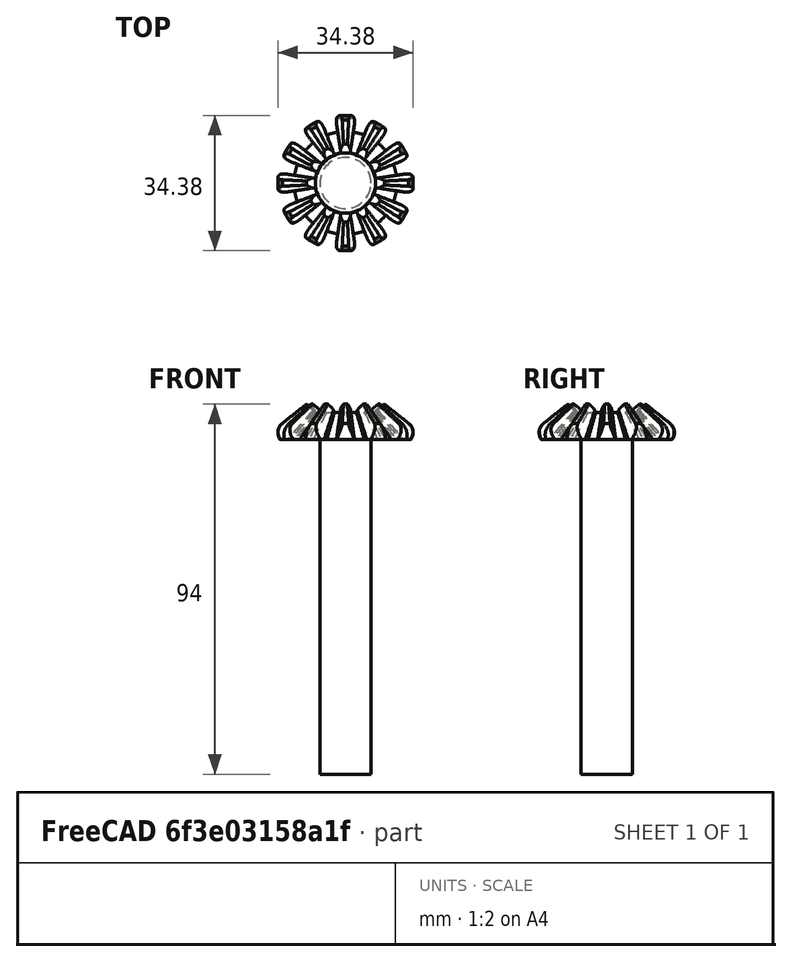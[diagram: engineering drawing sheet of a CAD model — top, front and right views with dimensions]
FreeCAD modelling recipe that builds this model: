
FCSTD DOCUMENT  (FreeCAD 1.0R39319 (Git))
Label: DG Krushna gearshaft
License: All rights reserved
LicenseURL: https://en.wikipedia.org/wiki/All_rights_reserved
objects: Sketcher::SketchObject×5, TechDraw::DrawViewDimension×5, TechDraw::DrawProjGroupItem×4, PartDesign::Groove×3, TechDraw::DrawSVGTemplate×2, TechDraw::DrawProjGroup×2, TechDraw::DrawPage×2, Part::FeaturePython×1, PartDesign::FeatureBase×1, PartDesign::Pad×1, PartDesign::Body×1
note: 31 computed .brp shape members not serialized (recipe doc carries the construction recipe); baked Part::Feature solids carry a one-line shape summary decoded from their .brp

FEATURE [Part::FeaturePython] BevelGear  # WARN: FeaturePython — macro-defined, semantics opaque (R4)
  AttacherType = Attacher::AttachEngine3D
  angular_backlash = 0
  backlash = 0
  beta = 0
  clearance = 0.1
  dw = 33.6
  height = 9
  module = 2.8
  num_teeth = 12
  numpoints = 20
  pitch_angle = 45
  pressure_angle = 20
  reset_origin = true
  version = 1.3.0
  expr: angular_backlash = backlash / dw * 360 ° / pi
  expr: dw = num_teeth * module
FEATURE [PartDesign::FeatureBase] BaseFeature
  BaseFeature = -> BevelGear
  Suppressed = false
FEATURE [Sketcher::SketchObject] Sketch001
  ArcFitTolerance = 1e-06
  FullyConstrained = true
  MakeInternals = false
  MapMode = 5
  Placement = pos=(0,0,0) rot=(1,0,0;3.14159rad)
  sketch-geometry (2):
    g0: Circle CenterX=0 CenterY=0 CenterZ=0 NormalX=0 NormalY=0 NormalZ=1 AngleXU=0 Radius=16.6594
    g1: Circle CenterX=0 CenterY=0 CenterZ=0 NormalX=0 NormalY=0 NormalZ=1 AngleXU=0 Radius=24.4797
  constraints (4):
    c: Coincident(g0,g-1)
    c: PointOnObject(g-4,g0)
    c: Coincident(g1,g0)
    c: PointOnObject(g-3,g1)
FEATURE [Sketcher::SketchObject] Sketch002
  ArcFitTolerance = 1e-06
  AttachmentSupport = -> [YZ_Plane]
  ExternalGeometry = -> [Sketch001]
  FullyConstrained = true
  MakeInternals = false
  MapMode = 5
  Placement = pos=(0,0,0) rot=(0.57735,0.57735,0.57735;2.0944rad)
  sketch-geometry (3):
    g0: LineSegment StartX=16.6594 StartY=0 StartZ=0 EndX=24.4797 EndY=7.82034 EndZ=0
    g1: LineSegment StartX=24.4797 StartY=0 StartZ=0 EndX=24.4797 EndY=7.82034 EndZ=0
    g2: LineSegment StartX=24.4797 StartY=0 StartZ=0 EndX=16.6594 EndY=0 EndZ=0
  constraints (7):
    c: Coincident(g0,g-3)
    c: Coincident(g1,g-4)
    c: Vertical(g1)
    c: Coincident(g0,g1)
    c: Angle(g-4,g0) = 0.785398
    c: Coincident(g2,g1)
    c: Coincident(g2,g0)
FEATURE [PartDesign::Groove] Groove001
  Angle = 360
  Angle2 = 60
  Axis = (0,0,1)
  Base = (0,0,0)
  BaseFeature = -> BaseFeature
  Profile = -> Sketch002
  ReferenceAxis = -> Sketch002 [V_Axis]
  Refine = true
  Suppressed = false
  Type = 0
FEATURE [Sketcher::SketchObject] Sketch
  ArcFitTolerance = 1e-06
  AttachmentSupport = -> [XZ_Plane]
  ExternalGeometry = -> [Groove001]
  FullyConstrained = true
  MakeInternals = false
  MapMode = 5
  Placement = pos=(0,0,0) rot=(1,0,0;1.5708rad)
  sketch-geometry (4):
    g0: LineSegment StartX=9.88232 StartY=9 StartZ=0 EndX=0 EndY=9 EndZ=0
    g1: LineSegment StartX=9.88232 StartY=9 StartZ=0 EndX=7.63232 EndY=6.75 EndZ=0
    g2: LineSegment StartX=7.63232 StartY=6.75 StartZ=0 EndX=0 EndY=6.75 EndZ=0
    g3: LineSegment StartX=0 StartY=9 StartZ=0 EndX=0 EndY=6.75 EndZ=0
  constraints (11):
    c: Coincident(g0,g-3)
    c: PointOnObject(g0,g-2)
    c: Horizontal(g0)
    c: Coincident(g1,g0)
    c: Coincident(g2,g1)
    c: Horizontal(g2)
    c: Coincident(g3,g0)
    c: Coincident(g3,g2)
    c: Vertical(g3)
    c: Angle(g0,g1) = 0.785398
    c: DistanceY(g3,g3) = 2.25
FEATURE [PartDesign::Groove] Groove
  Angle = 360
  Angle2 = 60
  Axis = (0,2e-16,1)
  Base = (0,0,0)
  BaseFeature = -> Groove001
  Profile = -> Sketch
  ReferenceAxis = -> Sketch [V_Axis]
  Refine = true
  Suppressed = false
  Type = 0
FEATURE [Sketcher::SketchObject] Sketch003
  ArcFitTolerance = 1e-06
  FullyConstrained = true
  MakeInternals = false
  MapMode = 5
  Placement = pos=(0,0,0) rot=(1,0,0;3.14159rad)
  sketch-geometry (1):
    g0: Circle CenterX=0 CenterY=0 CenterZ=0 NormalX=0 NormalY=0 NormalZ=1 AngleXU=0 Radius=6.5
  constraints (2):
    c: Diameter(g0) = 13
    c: Coincident(g0,g-1)
FEATURE [PartDesign::Pad] Pad
  BaseFeature = -> Groove
  Direction = (0,-1e-16,-1)
  Length = 85
  Length2 = 10
  Profile = -> Sketch003
  ReferenceAxis = -> Sketch003 [N_Axis]
  Refine = true
  Suppressed = false
  Type = 0
FEATURE [Sketcher::SketchObject] Sketch004
  ArcFitTolerance = 1e-06
  AttachmentSupport = -> [YZ_Plane]
  ExternalGeometry = -> [Pad]
  FullyConstrained = true
  MakeInternals = false
  MapMode = 5
  Placement = pos=(0,0,0) rot=(0.57735,0.57735,0.57735;2.0944rad)
  sketch-geometry (5):
    g0: LineSegment StartX=18.6998 StartY=2.04045 StartZ=0 EndX=16.314 EndY=-0.345337 EndZ=0
    g1: ArcOfCircle CenterX=14.1927 CenterY=1.77598 CenterZ=0 NormalX=0 NormalY=0 NormalZ=1 AngleXU=0 Radius=3 StartAngle=5.49779 EndAngle=7.18581
    g2: LineSegment StartX=16.0514 StartY=4.13084 StartZ=0 EndX=18.1868 EndY=6.26631 EndZ=0
    g3: LineSegment StartX=18.1868 StartY=6.26631 StartZ=0 EndX=20.8353 EndY=4.17592 EndZ=0
    g4: LineSegment StartX=20.8353 StartY=4.17592 StartZ=0 EndX=18.6998 EndY=2.04045 EndZ=0
  constraints (13):
    c: Coincident(g0,g-4)
    c: Tangent(g1,g-4)
    c: Tangent(g0,g1) = 1.5708
    c: Radius(g1) = 3
    c: Coincident(g2,g1)
    c: Coincident(g3,g2)
    c: Coincident(g4,g0)
    c: Coincident(g4,g3)
    c: Equal(g2,g4)
    c: Parallel(g0,g4)
    c: Parallel(g2,g0)
    c: Tangent(g1,g-3) = 1.5708
    c: Distance(g2,g2) = 3.02
FEATURE [PartDesign::Groove] Groove002
  Angle = 360
  Angle2 = 60
  Axis = (0,0,1)
  Base = (0,0,0)
  BaseFeature = -> Pad
  Profile = -> Sketch004
  ReferenceAxis = -> Sketch004 [V_Axis]
  Refine = true
  Suppressed = false
  Type = 0
FEATURE [PartDesign::Body] Body
  AllowCompound = false
  BaseFeature = -> BevelGear
  Group = -> [BaseFeature,Sketch001,Sketch002,Groove001,Sketch,Groove,Sketch003,Pad,Sketch004,Groove002]
  Origin = -> Origin
  Tip = -> Groove002
FEATURE [TechDraw::DrawSVGTemplate] Template
  Height = 210
  Orientation = 1
  Template = C:/Program Files/FreeCAD 1.0/data/Mod/TechDraw/Templates/A4_Landscape_TD.svg
  Width = 297
FEATURE [TechDraw::DrawProjGroupItem] View  label="Front"
  CoarseView = false
  Direction = (0,-1,0)
  Focus = 100
  HardHidden = false
  IsoCount = 0
  IsoHidden = false
  IsoVisible = false
  LockPosition = true
  Perspective = false
  Rotation = 0
  RotationVector = (1,0,0)
  ScaleType = 2
  ScrubCount = 1
  SeamHidden = false
  SeamVisible = false
  SmoothHidden = false
  SmoothVisible = true
  Source = -> [Body]
  Type = 0
  X = 0
  XDirection = (1,0,0)
  Y = 0
FEATURE [TechDraw::DrawProjGroupItem] ProjItem  label="Top"
  CoarseView = false
  Direction = (0,0,1)
  Focus = 100
  HardHidden = false
  IsoCount = 0
  IsoHidden = false
  IsoVisible = false
  LockPosition = false
  Perspective = false
  Rotation = 0
  RotationVector = (1,0,0)
  ScaleType = 0
  ScrubCount = 1
  SeamHidden = false
  SeamVisible = false
  SmoothHidden = false
  SmoothVisible = true
  Source = -> [Body]
  Type = 4
  X = 0
  XDirection = (1,0,0)
  Y = -79.1927
FEATURE [TechDraw::DrawProjGroup] ProjGroup
  Anchor = -> View
  AutoDistribute = true
  LockPosition = false
  ProjectionType = 0
  Rotation = 0
  ScaleType = 0
  Source = -> [Body]
  Views = -> [View,ProjItem]
  X = 90.1708
  Y = 135.331
  spacingX = 15
  spacingY = 15
FEATURE [TechDraw::DrawViewDimension] Dimension
  AngleOverride = false
  Arbitrary = false
  ArbitraryTolerances = false
  BoxCorners = (2) [(-17.1927,-47,-1e-07),(17.1927,47,1e-07)]
  EqualTolerance = true
  ExtensionAngle = 0
  FormatSpec = %.2w
  FormatSpecOverTolerance = %+.2w
  FormatSpecUnderTolerance = %+.2w
  Inverted = false
  LineAngle = 0
  LockPosition = false
  MeasureType = 1
  OverTolerance = 0
  References2D = -> [View]
  Rotation = 0
  ScaleType = 0
  TheoreticalExact = false
  Type = 2
  UnderTolerance = 0
  X = 28.3171
  Y = -8.42043
FEATURE [TechDraw::DrawViewDimension] Dimension001
  AngleOverride = false
  Arbitrary = false
  ArbitraryTolerances = false
  BoxCorners = (2) [(-17.1927,-47,-1e-07),(17.1927,47,1e-07)]
  EqualTolerance = true
  ExtensionAngle = 0
  FormatSpec = %.2w
  FormatSpecOverTolerance = %+.2w
  FormatSpecUnderTolerance = %+.2w
  Inverted = false
  LineAngle = 0
  LockPosition = false
  MeasureType = 1
  OverTolerance = 0
  References2D = -> [View]
  Rotation = 0
  ScaleType = 0
  TheoreticalExact = false
  Type = 0
  UnderTolerance = 0
  X = -35.6201
  Y = -19.4382
FEATURE [TechDraw::DrawPage] Page
  KeepUpdated = true
  NextBalloonIndex = 1
  ProjectionType = 0
  Template = -> Template
  Views = -> [ProjGroup,Dimension,Dimension001]
FEATURE [TechDraw::DrawSVGTemplate] Template001
  EditableTexts = AuthorName=Krushna manwatkar; CheckDate=CHECK DATE; CreationDate=06-01-2026; DrawingNumber=NUMBER; FC-Title=DG Krushna gearshaft; SheetNumber=2 / 2; Subtitle=SUBTITLE; SupervisorName=SUPERVISOR NAME; Weight=WEIGHT; scale=1 : 1
  Height = 297
  Orientation = 1
  Template = C:/Program Files/FreeCAD 1.0/data/Mod/TechDraw/Templates/A3_Landscape_TD.svg
  Width = 420
FEATURE [TechDraw::DrawProjGroupItem] View001  label="Front001"
  CoarseView = false
  Direction = (0,-1,0)
  Focus = 100
  HardHidden = false
  IsoCount = 0
  IsoHidden = false
  IsoVisible = false
  LockPosition = true
  Perspective = false
  Rotation = 0
  RotationVector = (1,0,0)
  ScaleType = 2
  ScrubCount = 1
  SeamHidden = false
  SeamVisible = false
  SmoothHidden = false
  SmoothVisible = true
  Source = -> [Body]
  Type = 0
  X = 0
  XDirection = (1,0,0)
  Y = 0
FEATURE [TechDraw::DrawProjGroupItem] ProjItem001  label="Bottom"
  CoarseView = false
  Direction = (0,0,-1)
  Focus = 100
  HardHidden = false
  IsoCount = 0
  IsoHidden = false
  IsoVisible = false
  LockPosition = false
  Perspective = false
  Rotation = 0
  RotationVector = (1,0,0)
  ScaleType = 0
  ScrubCount = 1
  SeamHidden = false
  SeamVisible = false
  SmoothHidden = false
  SmoothVisible = true
  Source = -> [Body]
  Type = 5
  X = 0
  XDirection = (1,0,0)
  Y = -79.1927
FEATURE [TechDraw::DrawProjGroup] ProjGroup001
  Anchor = -> View001
  AutoDistribute = true
  LockPosition = false
  ProjectionType = 1
  Rotation = 0
  ScaleType = 0
  Source = -> [Body]
  Views = -> [View001,ProjItem001]
  X = 60.1329
  Y = 220.973
  spacingX = 15
  spacingY = 15
FEATURE [TechDraw::DrawViewDimension] Dimension002
  AngleOverride = false
  Arbitrary = false
  ArbitraryTolerances = false
  BoxCorners = (2) [(-17.1927,-47,-1e-07),(17.1927,47,1e-07)]
  EqualTolerance = true
  ExtensionAngle = 0
  FormatSpec = %.2w
  FormatSpecOverTolerance = %+.2w
  FormatSpecUnderTolerance = %+.2w
  Inverted = false
  LineAngle = 0
  LockPosition = false
  MeasureType = 1
  OverTolerance = 0
  References2D = -> [View001]
  Rotation = 0
  ScaleType = 0
  TheoreticalExact = false
  Type = 2
  UnderTolerance = 0
  X = 80.4674
  Y = 7.79749
FEATURE [TechDraw::DrawViewDimension] Dimension003
  AngleOverride = false
  Arbitrary = false
  ArbitraryTolerances = false
  BoxCorners = (2) [(-17.1927,-17.1927,-1e-07),(17.1927,17.1927,1e-07)]
  EqualTolerance = true
  ExtensionAngle = 0
  FormatSpec = ⌀%.2w
  FormatSpecOverTolerance = %+.2w
  FormatSpecUnderTolerance = %+.2w
  Inverted = false
  LineAngle = 0
  LockPosition = false
  MeasureType = 1
  OverTolerance = 0
  References2D = -> [ProjItem001]
  Rotation = 0
  ScaleType = 0
  TheoreticalExact = false
  Type = 5
  UnderTolerance = 0
  X = 78.2765
  Y = -14.8314
FEATURE [TechDraw::DrawViewDimension] Dimension004
  AngleOverride = false
  Arbitrary = false
  ArbitraryTolerances = false
  BoxCorners = (2) [(-17.1927,-17.1927,-1e-07),(17.1927,17.1927,1e-07)]
  EqualTolerance = true
  ExtensionAngle = 0
  FormatSpec = %.2w
  FormatSpecOverTolerance = %+.2w
  FormatSpecUnderTolerance = %+.2w
  Inverted = false
  LineAngle = 0
  LockPosition = false
  MeasureType = 1
  OverTolerance = 0
  References2D = -> [ProjItem001]
  Rotation = 0
  ScaleType = 0
  TheoreticalExact = false
  Type = 0
  UnderTolerance = 0
  X = 42.1397
  Y = -61.7469
FEATURE [TechDraw::DrawPage] Page001
  KeepUpdated = true
  NextBalloonIndex = 1
  ProjectionType = 0
  Template = -> Template001
  Views = -> [ProjGroup001,Dimension002,Dimension003,Dimension004]
